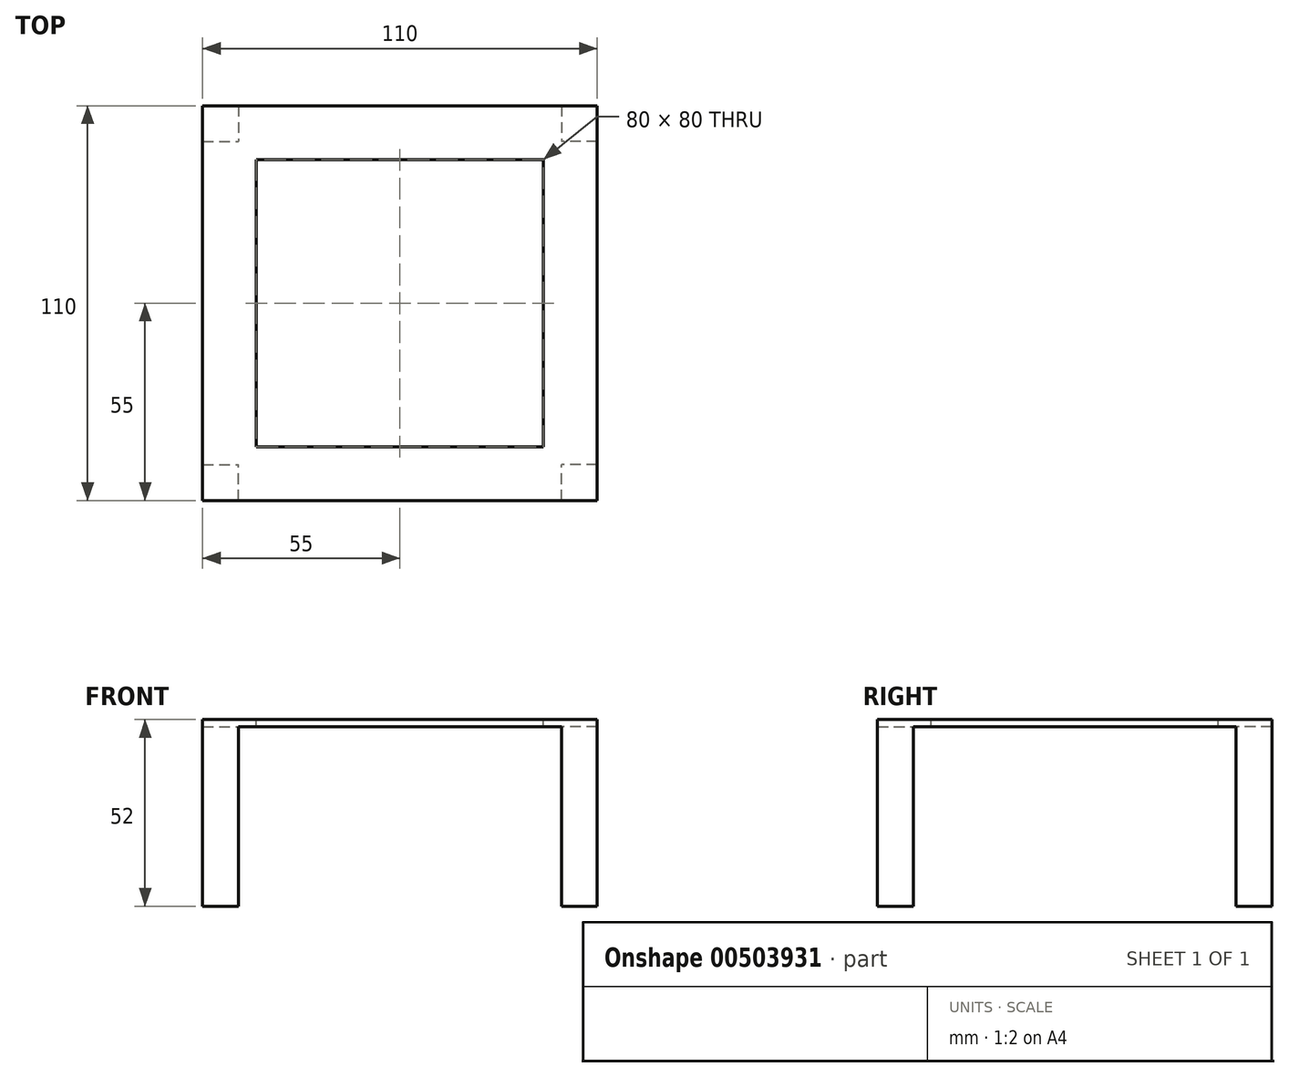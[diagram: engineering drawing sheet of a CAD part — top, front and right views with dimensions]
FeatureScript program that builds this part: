
annotation { "Feature Type Name" : "Feature", "Feature Type Description" : "" }
export const myFeature = defineFeature(function(context is Context, id is Id, definition is map)
    precondition{}
    {
        {
            var Q0;
            Q0=qCreatedBy(makeId("Top.planeOp"),FACE);
            var sketch = newSketch(context, id + "F0", { "sketchPlane" : qUnion([Q0])});
            skLineSegment(sketch, "E0.bottom", {"start": v(55, -55) * mm, "end": v(-55, -55) * mm});
            skLineSegment(sketch, "E0.top", {"start": v(55, 55) * mm, "end": v(-55, 55) * mm});
            skLineSegment(sketch, "E0.left", {"start": v(55, -55) * mm, "end": v(55, 55) * mm});
            skLineSegment(sketch, "E0.right", {"start": v(-55, -55) * mm, "end": v(-55, 55) * mm});
            skPoint(sketch, "E0.middle", {"position": v(0, 0) * mm});
            skSolve(sketch);
        }
        {
            var Q0;
            Q0=makeQuery(id+"F0.imprint","IMPRINT",FACE,{"disambiguationData":[TD([[makeQuery(id+"F0.imprint","IMPRINT",EDGE,{"derivedFrom":sQuery(id+"F0.wireOp",EDGE,"E0.bottom")}),-1.0]])]});
            extrude(context, id + "F1", {"entities" : qUnion([Q0]), "oppositeDirection" : true, "depth" : 2 * mm});
        }
        {
            var Q0;
            Q0=makeQuery(id+"F1.opExtrude","CAP_FACE",FACE,{"disambiguationData":[OSD([sQuery(id+"F0.wireOp",EDGE,"E0.bottom"),sQuery(id+"F0.wireOp",EDGE,"E0.top"),sQuery(id+"F0.wireOp",EDGE,"E0.left"),sQuery(id+"F0.wireOp",EDGE,"E0.right")])],"isStart":false});
            var sketch = newSketch(context, id + "F2", { "sketchPlane" : qUnion([Q0])});
            skLineSegment(sketch, "E1.bottom", {"start": v(-55, 55) * mm, "end": v(-45, 55) * mm});
            skLineSegment(sketch, "E1.top", {"start": v(-55, 45) * mm, "end": v(-45, 45) * mm});
            skLineSegment(sketch, "E1.left", {"start": v(-55, 55) * mm, "end": v(-55, 45) * mm});
            skLineSegment(sketch, "E1.right", {"start": v(-45, 55) * mm, "end": v(-45, 45) * mm});
            skLineSegment(sketch, "E2.bottom", {"start": v(55, 55) * mm, "end": v(45, 55) * mm});
            skLineSegment(sketch, "E2.top", {"start": v(55, 45) * mm, "end": v(45, 45) * mm});
            skLineSegment(sketch, "E2.left", {"start": v(55, 55) * mm, "end": v(55, 45) * mm});
            skLineSegment(sketch, "E2.right", {"start": v(45, 55) * mm, "end": v(45, 45) * mm});
            skLineSegment(sketch, "E3.bottom", {"start": v(55, -55) * mm, "end": v(45, -55) * mm});
            skLineSegment(sketch, "E3.top", {"start": v(55, -45) * mm, "end": v(45, -45) * mm});
            skLineSegment(sketch, "E3.left", {"start": v(55, -55) * mm, "end": v(55, -45) * mm});
            skLineSegment(sketch, "E3.right", {"start": v(45, -55) * mm, "end": v(45, -45) * mm});
            skLineSegment(sketch, "E4.bottom", {"start": v(-55, -55) * mm, "end": v(-45, -55) * mm});
            skLineSegment(sketch, "E4.top", {"start": v(-55, -45) * mm, "end": v(-45, -45) * mm});
            skLineSegment(sketch, "E4.left", {"start": v(-55, -55) * mm, "end": v(-55, -45) * mm});
            skLineSegment(sketch, "E4.right", {"start": v(-45, -55) * mm, "end": v(-45, -45) * mm});
            skSolve(sketch);
        }
        {
            var Q0;
            Q0=makeQuery(id+"F2.imprint","IMPRINT",FACE,{"disambiguationData":[TD([[makeQuery(id+"F2.imprint","IMPRINT",EDGE,{"derivedFrom":sQuery(id+"F2.wireOp",EDGE,"E4.bottom")}),-1.0]])]});
            var Q1;
            Q1=makeQuery(id+"F2.imprint","IMPRINT",FACE,{"disambiguationData":[TD([[makeQuery(id+"F2.imprint","IMPRINT",EDGE,{"derivedFrom":sQuery(id+"F2.wireOp",EDGE,"E1.bottom")}),1.0]])]});
            var Q2;
            Q2=makeQuery(id+"F2.imprint","IMPRINT",FACE,{"disambiguationData":[TD([[makeQuery(id+"F2.imprint","IMPRINT",EDGE,{"derivedFrom":sQuery(id+"F2.wireOp",EDGE,"E2.bottom")}),1.0]])]});
            var Q3;
            Q3=makeQuery(id+"F2.imprint","IMPRINT",FACE,{"disambiguationData":[TD([[makeQuery(id+"F2.imprint","IMPRINT",EDGE,{"derivedFrom":sQuery(id+"F2.wireOp",EDGE,"E3.bottom")}),-1.0]])]});
            extrude(context, id + "F3", {"entities" : qUnion([Q0, Q1, Q2, Q3]), "operationType" : NewBodyOperationType.ADD, "depth" : 50 * mm});
        }
        {
            var Q0;
            Q0=makeQuery(id+"F1.opExtrude","CAP_FACE",FACE,{"disambiguationData":[OSD([sQuery(id+"F0.wireOp",EDGE,"E0.bottom"),sQuery(id+"F0.wireOp",EDGE,"E0.top"),sQuery(id+"F0.wireOp",EDGE,"E0.left"),sQuery(id+"F0.wireOp",EDGE,"E0.right")])],"isStart":true});
            var sketch = newSketch(context, id + "F4", { "sketchPlane" : qUnion([Q0])});
            skLineSegment(sketch, "E5.bottom", {"start": v(-40, 40) * mm, "end": v(40, 40) * mm});
            skLineSegment(sketch, "E5.top", {"start": v(-40, -40) * mm, "end": v(40, -40) * mm});
            skLineSegment(sketch, "E5.left", {"start": v(-40, 40) * mm, "end": v(-40, -40) * mm});
            skLineSegment(sketch, "E5.right", {"start": v(40, 40) * mm, "end": v(40, -40) * mm});
            skSolve(sketch);
        }
        {
            var Q0;
            Q0=makeQuery(id+"F4.imprint","IMPRINT",FACE,{"disambiguationData":[TD([[makeQuery(id+"F4.imprint","IMPRINT",EDGE,{"derivedFrom":sQuery(id+"F4.wireOp",EDGE,"E5.bottom")}),-1.0]])]});
            extrude(context, id + "F5", {"entities" : qUnion([Q0]), "operationType" : NewBodyOperationType.REMOVE, "endBound" : BoundingType.THROUGH_ALL, "oppositeDirection" : true, "depth" : 21.6 * mm});
        }
    });
